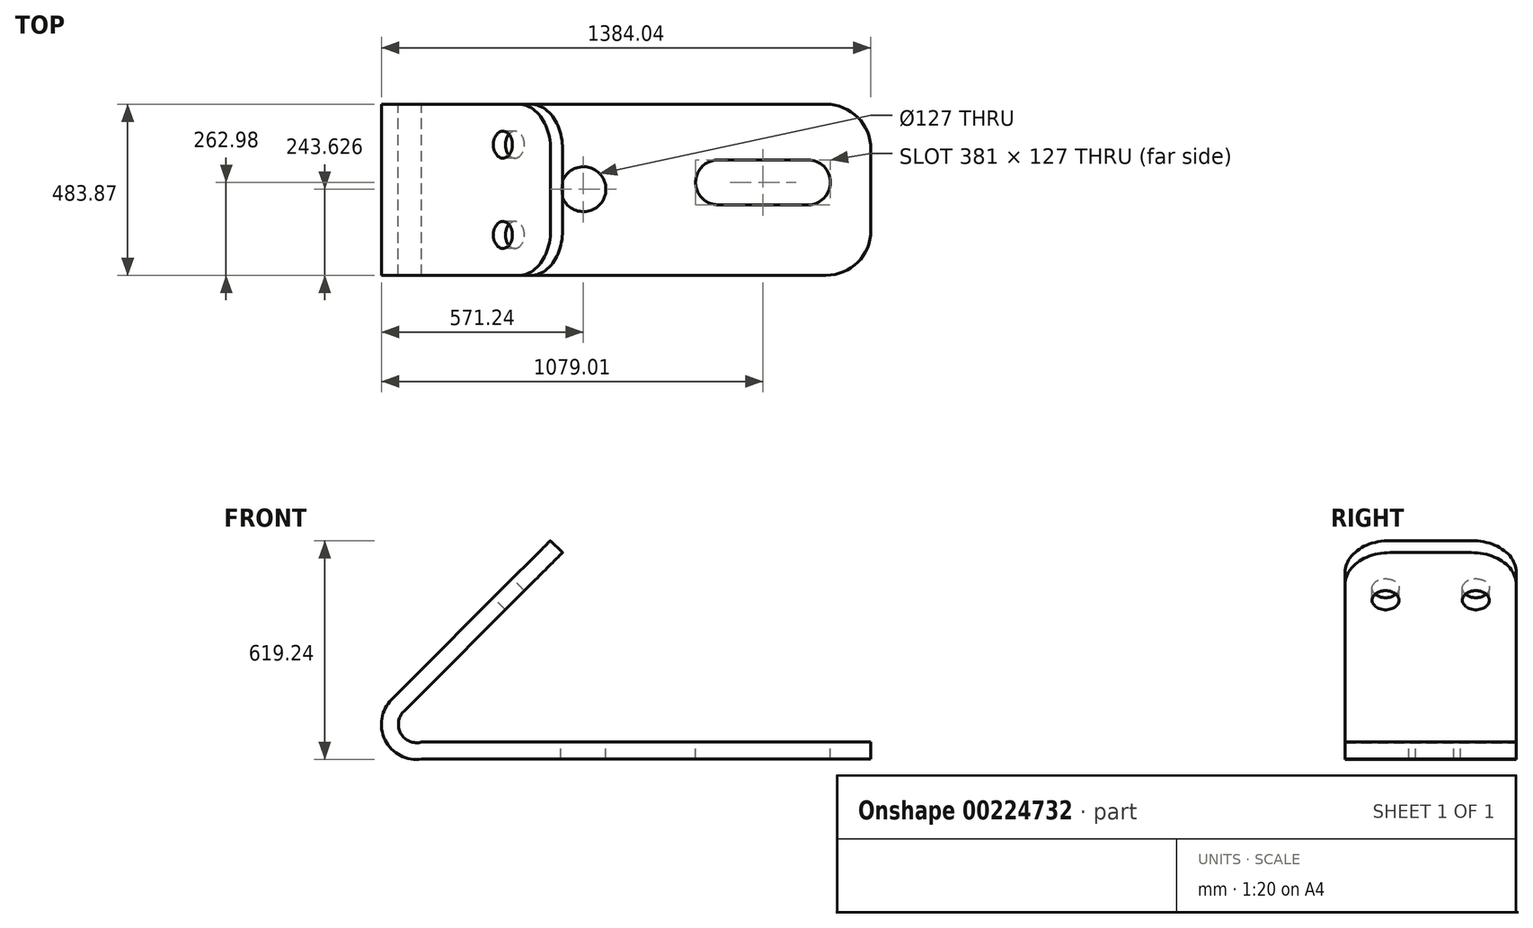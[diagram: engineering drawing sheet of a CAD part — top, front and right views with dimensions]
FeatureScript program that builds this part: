
annotation { "Feature Type Name" : "Feature", "Feature Type Description" : "" }
export const myFeature = defineFeature(function(context is Context, id is Id, definition is map)
    precondition{}
    {
        {
            var Q0;
            Q0=qCreatedBy(makeId("Front.planeOp"),FACE);
            var sketch = newSketch(context, id + "F0", { "sketchPlane" : qUnion([Q0])});
            skLineSegment(sketch, "E0.bottom", {"start": v(635, -24.13) * mm, "end": v(-635, -24.13) * mm});
            skLineSegment(sketch, "E0.top", {"start": v(635, 24.13) * mm, "end": v(-635, 24.13) * mm});
            skLineSegment(sketch, "E0.left", {"start": v(635, -24.13) * mm, "end": v(635, 24.13) * mm});
            skLineSegment(sketch, "E0.right", {"start": v(-635, -24.13) * mm, "end": v(-635, 24.13) * mm});
            skPoint(sketch, "E0.middle", {"position": v(0, 0) * mm});
            skLineSegment(sketch, "E1", {"start": v(-685.7, 110.95) * mm, "end": v(-236.7, 559.96) * mm});
            skLineSegment(sketch, "E2", {"start": v(-236.7, 559.96) * mm, "end": v(-270.82, 594.08) * mm});
            skLineSegment(sketch, "E3", {"start": v(-270.82, 594.08) * mm, "end": v(-719.83, 145.07) * mm});
            skArc(sketch, "E4", {"start": v(-719.83, 145.07) * mm, "mid": v(-738.46, 29.86) * mm, "end": v(-635, -24.13) * mm});
            skArc(sketch, "E5", {"start": v(-685.7, 110.95) * mm, "mid": v(-693.83, 47.98) * mm, "end": v(-635, 24.13) * mm});
            skSolve(sketch);
        }
        {
            var Q0;
            Q0 = qSketchRegion(id + "F0", true);
            extrude(context, id + "F1", {"entities" : qUnion([Q0]), "depth" : 483.87 * mm});
        }
        {
            var Q0;
            Q0=makeQuery(id+"F1.opExtrude","CAP_EDGE",EDGE,{"disambiguationData":[OSD([sQuery(id+"F0.wireOp",EDGE,"E2")])],"isStart":false});
            var Q1;
            Q1=makeQuery(id+"F1.opExtrude","CAP_EDGE",EDGE,{"disambiguationData":[OSD([sQuery(id+"F0.wireOp",EDGE,"E2")])],"isStart":true});
            fillet(context, id + "F2", {"entities" : qUnion([Q0, Q1]), "radius" : 127 * mm, "tangentPropagation" : true, "allowEdgeOverflow" : false});
        }
        {
            var Q0;
            Q0=makeQuery(id+"F1.opExtrude","SWEPT_FACE",FACE,{"disambiguationData":[OSD([sQuery(id+"F0.wireOp",EDGE,"E3")])]});
            var sketch = newSketch(context, id + "F3", { "sketchPlane" : qUnion([Q0])});
            skCircle(sketch, "E6", {"center": v(114.3, 38.08) * mm, "radius": 38.1 * mm});
            skCircle(sketch, "E7", {"center": v(369.57, 38.08) * mm, "radius": 38.1 * mm});
            skSolve(sketch);
        }
        {
            var Q0;
            Q0=makeQuery(id+"F3.imprint","IMPRINT",FACE,{"disambiguationData":[TD([[makeQuery(id+"F3.imprint","IMPRINT",EDGE,{"derivedFrom":sQuery(id+"F3.wireOp",EDGE,"E6")}),1.0]])]});
            var Q1;
            Q1=makeQuery(id+"F3.imprint","IMPRINT",FACE,{"disambiguationData":[TD([[makeQuery(id+"F3.imprint","IMPRINT",EDGE,{"derivedFrom":sQuery(id+"F3.wireOp",EDGE,"E7")}),1.0]])]});
            var Q2;
            Q2=sQuery(id+"F3.wireOp",EDGE,"E6");
            var Q3;
            Q3=sQuery(id+"F3.wireOp",EDGE,"E7");
            extrude(context, id + "F4", {"entities" : qUnion([Q0, Q1]), "operationType" : NewBodyOperationType.REMOVE, "surfaceEntities" : qUnion([Q2, Q3]), "oppositeDirection" : true, "depth" : 127 * mm});
        }
        {
            var Q0;
            Q0=makeQuery(id+"F1.opExtrude","SWEPT_FACE",FACE,{"disambiguationData":[OSD([sQuery(id+"F0.wireOp",EDGE,"E0.top")])]});
            var sketch = newSketch(context, id + "F5", { "sketchPlane" : qUnion([Q0])});
            skLineSegment(sketch, "E8.bottom", {"start": v(457.43, -284.39) * mm, "end": v(203.43, -284.39) * mm});
            skLineSegment(sketch, "E8.top", {"start": v(456.97, -157.39) * mm, "end": v(202.97, -157.39) * mm});
            skPoint(sketch, "E8.middle", {"position": v(330.2, -220.89) * mm});
            skArc(sketch, "E9", {"start": v(202.97, -157.39) * mm, "mid": v(139.47, -221.12) * mm, "end": v(203.43, -284.39) * mm});
            skArc(sketch, "E10", {"start": v(456.97, -157.39) * mm, "mid": v(520.47, -220.66) * mm, "end": v(457.43, -284.39) * mm});
            skCircle(sketch, "E11", {"center": v(-177.8, -240.24) * mm, "radius": 63.5 * mm});
            skSolve(sketch);
        }
        {
            var Q0;
            Q0=makeQuery(id+"F5.imprint","IMPRINT",FACE,{"disambiguationData":[TD([[makeQuery(id+"F5.imprint","IMPRINT",EDGE,{"derivedFrom":sQuery(id+"F5.wireOp",EDGE,"E8.bottom")}),-1.0]])]});
            var Q1;
            Q1=makeQuery(id+"F5.imprint","IMPRINT",FACE,{"disambiguationData":[TD([[makeQuery(id+"F5.imprint","IMPRINT",EDGE,{"derivedFrom":sQuery(id+"F5.wireOp",EDGE,"E11")}),1.0]])]});
            extrude(context, id + "F6", {"entities" : qUnion([Q0, Q1]), "operationType" : NewBodyOperationType.REMOVE, "oppositeDirection" : true, "depth" : 50.8 * mm});
        }
        {
            var Q0;
            Q0=makeQuery(id+"F1.opExtrude","CAP_EDGE",EDGE,{"disambiguationData":[OSD([sQuery(id+"F0.wireOp",EDGE,"E0.left")])],"isStart":false});
            var Q1;
            Q1=makeQuery(id+"F1.opExtrude","CAP_EDGE",EDGE,{"disambiguationData":[OSD([sQuery(id+"F0.wireOp",EDGE,"E0.left")])],"isStart":true});
            fillet(context, id + "F7", {"entities" : qUnion([Q0, Q1]), "radius" : 127 * mm, "tangentPropagation" : true, "allowEdgeOverflow" : false});
        }
    });
